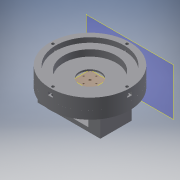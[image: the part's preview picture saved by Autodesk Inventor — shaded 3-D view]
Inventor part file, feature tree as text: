
AUTODESK INVENTOR PART (.ipt)
format: ipt  version: 2018 (Build 220112000, 112)  size: 299,520 bytes
history: native  units: mm
features: extrude x12, sketch x10, other x4, plane x2, pattern_circular x1
ambient origin geometry x8: Origin, YZ Plane, XZ Plane, XY Plane, X Axis, Y Axis, Z Axis, Center Point
bodies: Solid1 (feature_tree)
feature tree (29):
  extrude  "Extrusion1"  Depth=100.0mm
  extrude  "Extrusion2"  Depth=10.0mm TaperAngle=0.0deg
  sketch  "Sketch3"  dims[d2=14.0mm d3=0.0mm d4=10.0mm d5=0.0mm]
  extrude  "Extrusion3"  Depth=10.0mm
  extrude  "Extrusion4"  Depth=41.0mm
  extrude  "Extrusion5"  Depth=7.5mm
  extrude  "Extrusion6"  Depth=15.0mm
  extrude  "Extrusion7"  Depth=5.0mm TaperAngle=0.0deg
  plane  "Work Plane1"
  extrude  "Extrusion12"  Depth=25.0mm
  pattern_circular  "Circular Pattern1"  [2 undecoded]
  extrude  "Extrusion14"  Depth=5.0mm
  extrude  "Extrusion15"  Depth=5.0mm
  sketch  "Sketch20"  dims[d22=5.0mm d23=0.0mm]
  plane  "Plano de trabajo2"
  extrude  "Extrusión19"  Depth=6.0mm
  extrude  "Extrusión20"  Depth=6.0mm
  other  "Edición directa1"
  sketch  "Sketch1"  dims[d0=86.0mm d1=100.0mm]
  sketch  "Sketch4"  dims[d6=20.0mm d7=10.0mm]
  sketch  "Sketch5"  dims[d8=40.0mm d9=41.0mm]
  sketch  "Sketch6"  dims[d10=7.5mm d11=7.5mm]
  sketch  "Sketch12"  dims[d13=35.0mm d14=15.0mm]
  sketch  "Sketch14"  dims[d16=7.5mm d17=5.0mm d18=0.0mm]
  sketch  "Sketch17"  dims[d19=25.0mm d20=0.0mm d21=100.0mm]
  sketch  "Boceto21"  dims[d24=2.5mm d25=3.0mm d26=5.0mm d27=5.0mm d28=6.0mm d29=6.0mm d30=5.0mm d31=0.0mm d32=3.5mm d33=40.0mm d35=360.0deg d37=10.0mm d38=0.0mm d51=5.0mm d52=3.0mm d53=4.0mm d54=6.0mm d55=13.0mm d56=0.0mm d57=40.0mm d58=360.0deg d72=8.0mm d73=0.0mm d74=26.0mm d75=34.0mm d76=0.0mm d96=2.0mm d97=2.0mm d98=2.0mm d99=2.0mm d100=3.0mm d101=8.0mm d102=0.0mm d103=27.0mm d104=2.0mm d105=0.0mm d106=0.0mm d107=0.0mm d108=-3.0mm d109=0.0mm d110=0.0mm d111=-1.0mm d112=0.0mm d113=0.0mm d114=0.75mm]
  other  "Desplazar1"
  other  "Desplazar2"
  other  "Desplazar3"
note: 2 required parameter values undecoded (feature->parameter linkage not recoverable at this tier; creation-order binding heuristic only, values carry confidence <= 0.55)
